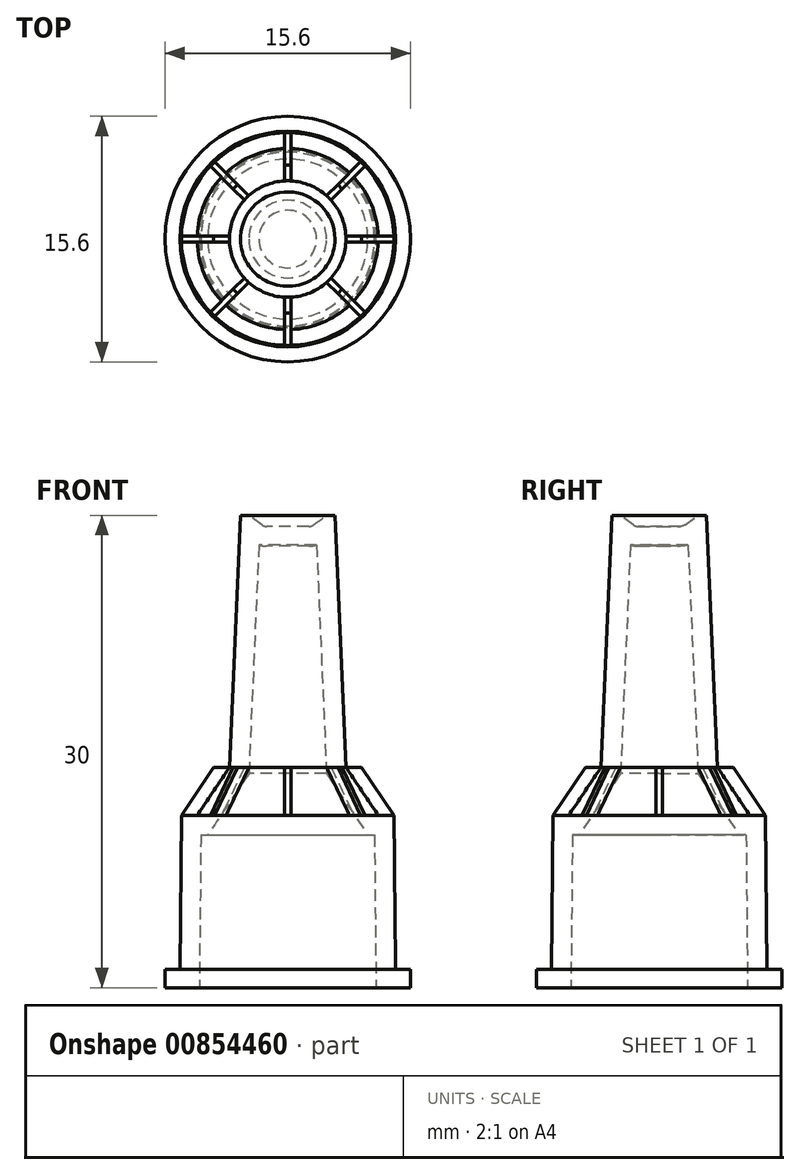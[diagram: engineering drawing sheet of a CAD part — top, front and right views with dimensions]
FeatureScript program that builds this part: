
annotation { "Feature Type Name" : "Feature", "Feature Type Description" : "" }
export const myFeature = defineFeature(function(context is Context, id is Id, definition is map)
    precondition{}
    {
        {
            var Q0;
            Q0=qCreatedBy(makeId("Front.planeOp"),FACE);
            var sketch = newSketch(context, id + "F0", { "sketchPlane" : qUnion([Q0])});
            skLineSegment(sketch, "E0", {"start": v(0, 0) * mm, "end": v(-7.8, 0) * mm});
            skLineSegment(sketch, "E1", {"start": v(-7.8, 0) * mm, "end": v(-7.8, 1.15) * mm});
            skLineSegment(sketch, "E2", {"start": v(-7.8, 1.15) * mm, "end": v(-6.85, 1.15) * mm});
            skLineSegment(sketch, "E3", {"start": v(-6.85, 1.15) * mm, "end": v(-6.75, 10.95) * mm});
            skLineSegment(sketch, "E4", {"start": v(-3.7, 14) * mm, "end": v(-3, 30) * mm});
            skLineSegment(sketch, "E5", {"start": v(-3, 30) * mm, "end": v(-2.6, 30) * mm});
            skLineSegment(sketch, "E6", {"start": v(0, 29.3) * mm, "end": v(0, 0) * mm});
            skLineSegment(sketch, "E7", {"start": v(-6.75, 10.95) * mm, "end": v(-5.75, 10.95) * mm});
            skLineSegment(sketch, "E8", {"start": v(-5.75, 10.95) * mm, "end": v(-3.7, 14) * mm});
            skLineSegment(sketch, "E9", {"start": v(-2.42, 29.95) * mm, "end": v(-1.63, 29.4) * mm});
            skLineSegment(sketch, "E10", {"start": v(-1.34, 29.3) * mm, "end": v(0, 29.3) * mm});
            skPoint(sketch, "E11.visualSharp", {"position": v(-1.5, 29.3) * mm});
            skArc(sketch, "E11.filletArc", {"start": v(-1.63, 29.4) * mm, "mid": v(-1.5, 29.32) * mm, "end": v(-1.34, 29.3) * mm});
            skPoint(sketch, "E12.visualSharp", {"position": v(-2.5, 30) * mm});
            skArc(sketch, "E12.filletArc", {"start": v(-2.42, 29.95) * mm, "mid": v(-2.5, 29.99) * mm, "end": v(-2.6, 30) * mm});
            skSolve(sketch);
        }
        {
            var Q0;
            Q0=qCreatedBy(makeId("Front.planeOp"),FACE);
            var sketch = newSketch(context, id + "F1", { "sketchPlane" : qUnion([Q0])});
            skLineSegment(sketch, "E13", {"start": v(-6.75, 10.95) * mm, "end": v(-5.55, 10.95) * mm});
            skLineSegment(sketch, "E14", {"start": v(-3.5, 14) * mm, "end": v(-4.7, 14) * mm});
            skLineSegment(sketch, "E15", {"start": v(-4.7, 14) * mm, "end": v(-6.75, 10.95) * mm});
            skLineSegment(sketch, "E16", {"start": v(0, 0) * mm, "end": v(0, 29.3) * mm});
            skLineSegment(sketch, "E17", {"start": v(-3.5, 14) * mm, "end": v(-5.55, 10.95) * mm});
            skSolve(sketch);
        }
        {
            var Q0;
            Q0 = qSketchRegion(id + "F1", true);
            extrude(context, id + "F2", {"entities" : qUnion([Q0]), "depth" : .4 * mm, "offsetDistance" : 25 * mm, "symmetric" : true});
        }
        {
            var Q0;
            Q0 = qSketchRegion(id + "F0", true);
            var Q1;
            Q1=sQuery(id+"F0.wireOp",EDGE,"E6");
            revolve(context, id + "F3", {"surfaceOperationType" : NewSurfaceOperationType.NEW, "entities" : qUnion([Q0]), "axis" : qUnion([Q1]), "revolveType" : RevolveType.FULL});
        }
        {
            var Q0;
            Q0=makeQuery(id+"F3.opRevolve","SWEPT_FACE",FACE,{"disambiguationData":[OSD([sQuery(id+"F0.wireOp",EDGE,"E0")])]});
            shell(context, id + "F4", {"entities" : qUnion([Q0]), "thickness" : 1.25 * mm});
        }
        {
            var Q0;
            Q0=makeQuery(id+"F2.opExtrude","SWEPT_BODY",BODY,{"disambiguationData":[OSD([sQuery(id+"F1.wireOp",EDGE,"E13"),sQuery(id+"F1.wireOp",EDGE,"tDyfTTnV-Kyan-QWxY-rI6f-kbWgb2c45UGB"),sQuery(id+"F1.wireOp",EDGE,"E14"),sQuery(id+"F1.wireOp",EDGE,"E15")])]});
            var Q1;
            Q1=sQuery(id+"F0.wireOp",EDGE,"E6");
            circularPattern(context, id + "F5", {"operationType" : NewBodyOperationType.ADD, "entities" : qUnion([Q0]), "axis" : qUnion([Q1]), "angle" : 360 * degree, "instanceCount" : 8, "equalSpace" : true});
        }
    });
